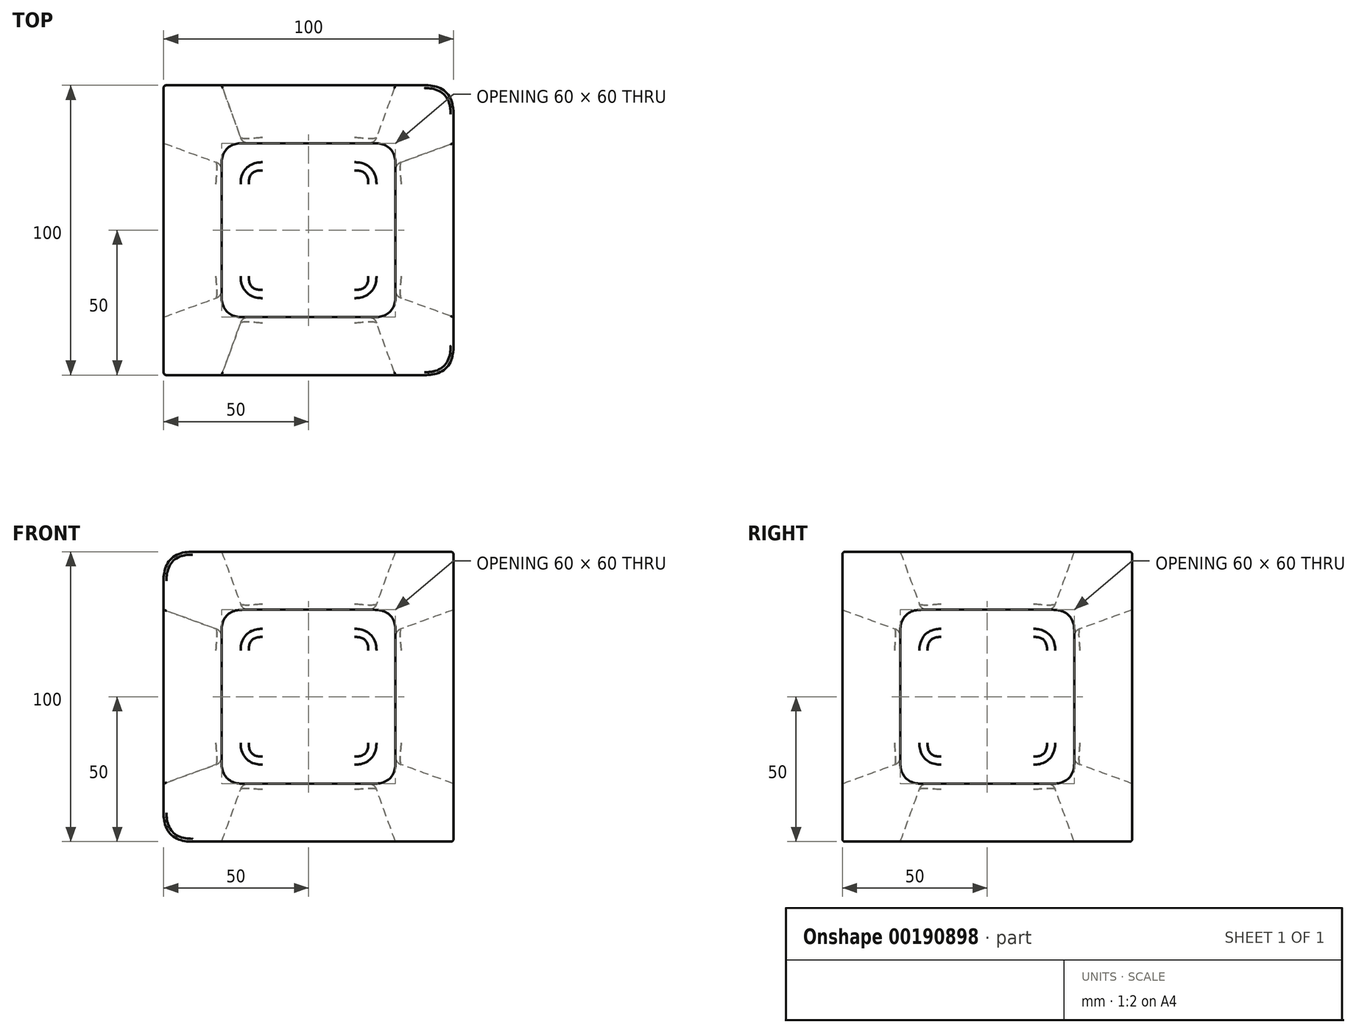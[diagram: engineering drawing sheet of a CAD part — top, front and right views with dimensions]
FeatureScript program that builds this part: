
annotation { "Feature Type Name" : "Feature", "Feature Type Description" : "" }
export const myFeature = defineFeature(function(context is Context, id is Id, definition is map)
    precondition{}
    {
        {
            var Q0;
            Q0=qCreatedBy(makeId("Top.planeOp"),FACE);
            var sketch = newSketch(context, id + "F0", { "sketchPlane" : qUnion([Q0])});
            skLineSegment(sketch, "E0.bottom", {"start": v(50, 50) * mm, "end": v(-50, 50) * mm});
            skLineSegment(sketch, "E0.top", {"start": v(50, -50) * mm, "end": v(-50, -50) * mm});
            skLineSegment(sketch, "E0.left", {"start": v(50, 50) * mm, "end": v(50, -50) * mm});
            skLineSegment(sketch, "E0.right", {"start": v(-50, 50) * mm, "end": v(-50, -50) * mm});
            skPoint(sketch, "E0.middle", {"position": v(0, 0) * mm});
            skSolve(sketch);
        }
        {
            var Q0;
            Q0 = qSketchRegion(id + "F0", true);
            extrude(context, id + "F1", {"entities" : qUnion([Q0]), "depth" : 100 * mm, "offsetDistance" : 25 * mm, "symmetric" : true});
        }
        {
            var Q0;
            Q0=makeQuery(id+"F1.opExtrude","CAP_FACE",FACE,{"disambiguationData":[OSD([sQuery(id+"F0.wireOp",EDGE,"E0.bottom"),sQuery(id+"F0.wireOp",EDGE,"E0.top"),sQuery(id+"F0.wireOp",EDGE,"E0.left"),sQuery(id+"F0.wireOp",EDGE,"E0.right")])],"isStart":false});
            var sketch = newSketch(context, id + "F2", { "sketchPlane" : qUnion([Q0])});
            skLineSegment(sketch, "E1.0", {"start": v(30, 30) * mm, "end": v(-30, 30) * mm});
            skLineSegment(sketch, "E1.1", {"start": v(30, 30) * mm, "end": v(30, -30) * mm});
            skLineSegment(sketch, "E1.2", {"start": v(30, -30) * mm, "end": v(-30, -30) * mm});
            skLineSegment(sketch, "E1.3", {"start": v(-30, 30) * mm, "end": v(-30, -30) * mm});
            skSolve(sketch);
        }
        {
            var Q0;
            Q0 = qSketchRegion(id + "F2", true);
            extrude(context, id + "F3", {"entities" : qUnion([Q0]), "operationType" : NewBodyOperationType.REMOVE, "oppositeDirection" : true, "depth" : 20 * mm, "offsetDistance" : 25 * mm, "hasDraft" : true, "draftAngle" : 20 * degree, "draftPullDirection" : true});
        }
        {
            var Q0;
            Q0=qCreatedBy(makeId("Top.planeOp"),FACE);
            var sketch = newSketch(context, id + "F4", { "sketchPlane" : qUnion([Q0])});
            skLineSegment(sketch, "E2", {"start": v(0, -64.23) * mm, "end": v(0, 63.51) * mm, "construction": true});
            skLineSegment(sketch, "E3", {"start": v(-60.37, 0) * mm, "end": v(65.94, 0) * mm, "construction": true});
            skSolve(sketch);
        }
        {
            var Q0;
            Q0=makeQuery(id+"F3.boolean.opBoolean","COPY",FACE,{"derivedFrom":makeQuery(id+"F3.opExtrude","CAP_FACE",FACE,{"disambiguationData":[OSD([sQuery(id+"F2.wireOp",EDGE,"E1.0"),sQuery(id+"F2.wireOp",EDGE,"E1.1"),sQuery(id+"F2.wireOp",EDGE,"E1.2"),sQuery(id+"F2.wireOp",EDGE,"E1.3")])],"isStart":false})});
            var Q1;
            Q1=makeQuery(id+"F3.boolean.opBoolean","COPY",FACE,{"derivedFrom":makeQuery(id+"F3.opExtrude","SWEPT_FACE",FACE,{"disambiguationData":[OSD([sQuery(id+"F2.wireOp",EDGE,"E1.3")])]})});
            var Q2;
            Q2=makeQuery(id+"F3.boolean.opBoolean","COPY",FACE,{"derivedFrom":makeQuery(id+"F3.opExtrude","SWEPT_FACE",FACE,{"disambiguationData":[OSD([sQuery(id+"F2.wireOp",EDGE,"E1.0")])]})});
            var Q3;
            Q3=makeQuery(id+"F3.boolean.opBoolean","COPY",FACE,{"derivedFrom":makeQuery(id+"F3.opExtrude","SWEPT_FACE",FACE,{"disambiguationData":[OSD([sQuery(id+"F2.wireOp",EDGE,"E1.1")])]})});
            var Q4;
            Q4=makeQuery(id+"F3.boolean.opBoolean","COPY",FACE,{"derivedFrom":makeQuery(id+"F3.opExtrude","SWEPT_FACE",FACE,{"disambiguationData":[OSD([sQuery(id+"F2.wireOp",EDGE,"E1.2")])]})});
            var Q5;
            Q5=sQuery(id+"F4.wireOp",EDGE,"E3");
            circularPattern(context, id + "F5", {"patternType" : PatternType.FACE, "faces" : qUnion([Q0, Q1, Q2, Q3, Q4]), "axis" : qUnion([Q5]), "angle" : 360 * degree, "instanceCount" : 4, "equalSpace" : true});
        }
        {
            var Q0;
            Q0=makeQuery(id+"F3.boolean.opBoolean","COPY",FACE,{"derivedFrom":makeQuery(id+"F3.opExtrude","CAP_FACE",FACE,{"disambiguationData":[OSD([sQuery(id+"F2.wireOp",EDGE,"E1.0"),sQuery(id+"F2.wireOp",EDGE,"E1.1"),sQuery(id+"F2.wireOp",EDGE,"E1.2"),sQuery(id+"F2.wireOp",EDGE,"E1.3")])],"isStart":false})});
            var Q1;
            Q1=makeQuery(id+"F3.boolean.opBoolean","COPY",FACE,{"derivedFrom":makeQuery(id+"F3.opExtrude","SWEPT_FACE",FACE,{"disambiguationData":[OSD([sQuery(id+"F2.wireOp",EDGE,"E1.3")])]})});
            var Q2;
            Q2=makeQuery(id+"F3.boolean.opBoolean","COPY",FACE,{"derivedFrom":makeQuery(id+"F3.opExtrude","SWEPT_FACE",FACE,{"disambiguationData":[OSD([sQuery(id+"F2.wireOp",EDGE,"E1.0")])]})});
            var Q3;
            Q3=makeQuery(id+"F3.boolean.opBoolean","COPY",FACE,{"derivedFrom":makeQuery(id+"F3.opExtrude","SWEPT_FACE",FACE,{"disambiguationData":[OSD([sQuery(id+"F2.wireOp",EDGE,"E1.1")])]})});
            var Q4;
            Q4=makeQuery(id+"F3.boolean.opBoolean","COPY",FACE,{"derivedFrom":makeQuery(id+"F3.opExtrude","SWEPT_FACE",FACE,{"disambiguationData":[OSD([sQuery(id+"F2.wireOp",EDGE,"E1.2")])]})});
            var Q5;
            Q5=sQuery(id+"F4.wireOp",EDGE,"E2");
            circularPattern(context, id + "F6", {"patternType" : PatternType.FACE, "faces" : qUnion([Q0, Q1, Q2, Q3, Q4]), "axis" : qUnion([Q5]), "angle" : 90 * degree, "instanceCount" : 2, "equalSpace" : true});
        }
        {
            var Q0;
            Q0=makeQuery(id+"F6.opPattern","COPY",FACE,{"derivedFrom":makeQuery(id+"F3.boolean.opBoolean","COPY",FACE,{"derivedFrom":makeQuery(id+"F3.opExtrude","CAP_FACE",FACE,{"disambiguationData":[OSD([sQuery(id+"F2.wireOp",EDGE,"E1.0"),sQuery(id+"F2.wireOp",EDGE,"E1.1"),sQuery(id+"F2.wireOp",EDGE,"E1.2"),sQuery(id+"F2.wireOp",EDGE,"E1.3")])],"isStart":false})}),"instanceName":"1"});
            var Q1;
            Q1=makeQuery(id+"F6.opPattern","COPY",FACE,{"derivedFrom":makeQuery(id+"F3.boolean.opBoolean","COPY",FACE,{"derivedFrom":makeQuery(id+"F3.opExtrude","SWEPT_FACE",FACE,{"disambiguationData":[OSD([sQuery(id+"F2.wireOp",EDGE,"E1.3")])]})}),"instanceName":"1"});
            var Q2;
            Q2=makeQuery(id+"F6.opPattern","COPY",FACE,{"derivedFrom":makeQuery(id+"F3.boolean.opBoolean","COPY",FACE,{"derivedFrom":makeQuery(id+"F3.opExtrude","SWEPT_FACE",FACE,{"disambiguationData":[OSD([sQuery(id+"F2.wireOp",EDGE,"E1.0")])]})}),"instanceName":"1"});
            var Q3;
            Q3=makeQuery(id+"F6.opPattern","COPY",FACE,{"derivedFrom":makeQuery(id+"F3.boolean.opBoolean","COPY",FACE,{"derivedFrom":makeQuery(id+"F3.opExtrude","SWEPT_FACE",FACE,{"disambiguationData":[OSD([sQuery(id+"F2.wireOp",EDGE,"E1.2")])]})}),"instanceName":"1"});
            var Q4;
            Q4=makeQuery(id+"F6.opPattern","COPY",FACE,{"derivedFrom":makeQuery(id+"F3.boolean.opBoolean","COPY",FACE,{"derivedFrom":makeQuery(id+"F3.opExtrude","SWEPT_FACE",FACE,{"disambiguationData":[OSD([sQuery(id+"F2.wireOp",EDGE,"E1.1")])]})}),"instanceName":"1"});
            var Q5;
            Q5=qCreatedBy(makeId("Right.planeOp"),FACE);
            mirror(context, id + "F7", {"patternType" : MirrorType.FACE, "faces" : qUnion([Q0, Q1, Q2, Q3, Q4]), "mirrorPlane" : qUnion([Q5])});
        }
        {
            var Q0;
            Q0=makeQuery(id+"F3.boolean.opBoolean","COPY",EDGE,{"derivedFrom":makeQuery(id+"F3.opExtrude","SWEPT_EDGE",EDGE,{"disambiguationData":[OSD([sQuery(id+"F2.wireOp",EDGE,"E1.0"),sQuery(id+"F2.wireOp",EDGE,"E1.3")])]})});
            var Q1;
            Q1=makeQuery(id+"F3.boolean.opBoolean","COPY",EDGE,{"derivedFrom":makeQuery(id+"F3.opExtrude","SWEPT_EDGE",EDGE,{"disambiguationData":[OSD([sQuery(id+"F2.wireOp",EDGE,"E1.0"),sQuery(id+"F2.wireOp",EDGE,"E1.1")])]})});
            var Q2;
            Q2=makeQuery(id+"F3.boolean.opBoolean","COPY",EDGE,{"derivedFrom":makeQuery(id+"F3.opExtrude","SWEPT_EDGE",EDGE,{"disambiguationData":[OSD([sQuery(id+"F2.wireOp",EDGE,"E1.2"),sQuery(id+"F2.wireOp",EDGE,"E1.3")])]})});
            var Q3;
            Q3=makeQuery(id+"F3.boolean.opBoolean","COPY",EDGE,{"derivedFrom":makeQuery(id+"F3.opExtrude","SWEPT_EDGE",EDGE,{"disambiguationData":[OSD([sQuery(id+"F2.wireOp",EDGE,"E1.1"),sQuery(id+"F2.wireOp",EDGE,"E1.2")])]})});
            var Q4;
            Q4=makeQuery(id+"F5.opPattern","COPY",EDGE,{"derivedFrom":makeQuery(id+"F3.boolean.opBoolean","COPY",EDGE,{"derivedFrom":makeQuery(id+"F3.opExtrude","SWEPT_EDGE",EDGE,{"disambiguationData":[OSD([sQuery(id+"F2.wireOp",EDGE,"E1.0"),sQuery(id+"F2.wireOp",EDGE,"E1.3")])]})}),"instanceName":"1"});
            var Q5;
            Q5=makeQuery(id+"F5.opPattern","COPY",EDGE,{"derivedFrom":makeQuery(id+"F3.boolean.opBoolean","COPY",EDGE,{"derivedFrom":makeQuery(id+"F3.opExtrude","SWEPT_EDGE",EDGE,{"disambiguationData":[OSD([sQuery(id+"F2.wireOp",EDGE,"E1.0"),sQuery(id+"F2.wireOp",EDGE,"E1.1")])]})}),"instanceName":"1"});
            var Q6;
            Q6=makeQuery(id+"F5.opPattern","COPY",EDGE,{"derivedFrom":makeQuery(id+"F3.boolean.opBoolean","COPY",EDGE,{"derivedFrom":makeQuery(id+"F3.opExtrude","SWEPT_EDGE",EDGE,{"disambiguationData":[OSD([sQuery(id+"F2.wireOp",EDGE,"E1.1"),sQuery(id+"F2.wireOp",EDGE,"E1.2")])]})}),"instanceName":"1"});
            var Q7;
            Q7=makeQuery(id+"F5.opPattern","COPY",EDGE,{"derivedFrom":makeQuery(id+"F3.boolean.opBoolean","COPY",EDGE,{"derivedFrom":makeQuery(id+"F3.opExtrude","SWEPT_EDGE",EDGE,{"disambiguationData":[OSD([sQuery(id+"F2.wireOp",EDGE,"E1.2"),sQuery(id+"F2.wireOp",EDGE,"E1.3")])]})}),"instanceName":"1"});
            var Q8;
            Q8=makeQuery(id+"F5.opPattern","COPY",EDGE,{"derivedFrom":makeQuery(id+"F3.boolean.opBoolean","COPY",EDGE,{"derivedFrom":makeQuery(id+"F3.opExtrude","SWEPT_EDGE",EDGE,{"disambiguationData":[OSD([sQuery(id+"F2.wireOp",EDGE,"E1.0"),sQuery(id+"F2.wireOp",EDGE,"E1.1")])]})}),"instanceName":"2"});
            var Q9;
            Q9=makeQuery(id+"F5.opPattern","COPY",EDGE,{"derivedFrom":makeQuery(id+"F3.boolean.opBoolean","COPY",EDGE,{"derivedFrom":makeQuery(id+"F3.opExtrude","SWEPT_EDGE",EDGE,{"disambiguationData":[OSD([sQuery(id+"F2.wireOp",EDGE,"E1.0"),sQuery(id+"F2.wireOp",EDGE,"E1.3")])]})}),"instanceName":"2"});
            var Q10;
            Q10=makeQuery(id+"F5.opPattern","COPY",EDGE,{"derivedFrom":makeQuery(id+"F3.boolean.opBoolean","COPY",EDGE,{"derivedFrom":makeQuery(id+"F3.opExtrude","SWEPT_EDGE",EDGE,{"disambiguationData":[OSD([sQuery(id+"F2.wireOp",EDGE,"E1.2"),sQuery(id+"F2.wireOp",EDGE,"E1.3")])]})}),"instanceName":"2"});
            var Q11;
            Q11=makeQuery(id+"F5.opPattern","COPY",EDGE,{"derivedFrom":makeQuery(id+"F3.boolean.opBoolean","COPY",EDGE,{"derivedFrom":makeQuery(id+"F3.opExtrude","SWEPT_EDGE",EDGE,{"disambiguationData":[OSD([sQuery(id+"F2.wireOp",EDGE,"E1.1"),sQuery(id+"F2.wireOp",EDGE,"E1.2")])]})}),"instanceName":"2"});
            var Q12;
            Q12=makeQuery(id+"F5.opPattern","COPY",EDGE,{"derivedFrom":makeQuery(id+"F3.boolean.opBoolean","COPY",EDGE,{"derivedFrom":makeQuery(id+"F3.opExtrude","SWEPT_EDGE",EDGE,{"disambiguationData":[OSD([sQuery(id+"F2.wireOp",EDGE,"E1.0"),sQuery(id+"F2.wireOp",EDGE,"E1.1")])]})}),"instanceName":"3"});
            var Q13;
            Q13=makeQuery(id+"F5.opPattern","COPY",EDGE,{"derivedFrom":makeQuery(id+"F3.boolean.opBoolean","COPY",EDGE,{"derivedFrom":makeQuery(id+"F3.opExtrude","SWEPT_EDGE",EDGE,{"disambiguationData":[OSD([sQuery(id+"F2.wireOp",EDGE,"E1.0"),sQuery(id+"F2.wireOp",EDGE,"E1.3")])]})}),"instanceName":"3"});
            var Q14;
            Q14=makeQuery(id+"F5.opPattern","COPY",EDGE,{"derivedFrom":makeQuery(id+"F3.boolean.opBoolean","COPY",EDGE,{"derivedFrom":makeQuery(id+"F3.opExtrude","SWEPT_EDGE",EDGE,{"disambiguationData":[OSD([sQuery(id+"F2.wireOp",EDGE,"E1.2"),sQuery(id+"F2.wireOp",EDGE,"E1.3")])]})}),"instanceName":"3"});
            var Q15;
            Q15=makeQuery(id+"F5.opPattern","COPY",EDGE,{"derivedFrom":makeQuery(id+"F3.boolean.opBoolean","COPY",EDGE,{"derivedFrom":makeQuery(id+"F3.opExtrude","SWEPT_EDGE",EDGE,{"disambiguationData":[OSD([sQuery(id+"F2.wireOp",EDGE,"E1.1"),sQuery(id+"F2.wireOp",EDGE,"E1.2")])]})}),"instanceName":"3"});
            var Q16;
            Q16=makeQuery(id+"F6.opPattern","COPY",EDGE,{"derivedFrom":makeQuery(id+"F3.boolean.opBoolean","COPY",EDGE,{"derivedFrom":makeQuery(id+"F3.opExtrude","SWEPT_EDGE",EDGE,{"disambiguationData":[OSD([sQuery(id+"F2.wireOp",EDGE,"E1.1"),sQuery(id+"F2.wireOp",EDGE,"E1.2")])]})}),"instanceName":"1"});
            var Q17;
            Q17=makeQuery(id+"F6.opPattern","COPY",EDGE,{"derivedFrom":makeQuery(id+"F3.boolean.opBoolean","COPY",EDGE,{"derivedFrom":makeQuery(id+"F3.opExtrude","SWEPT_EDGE",EDGE,{"disambiguationData":[OSD([sQuery(id+"F2.wireOp",EDGE,"E1.0"),sQuery(id+"F2.wireOp",EDGE,"E1.1")])]})}),"instanceName":"1"});
            var Q18;
            Q18=makeQuery(id+"F6.opPattern","COPY",EDGE,{"derivedFrom":makeQuery(id+"F3.boolean.opBoolean","COPY",EDGE,{"derivedFrom":makeQuery(id+"F3.opExtrude","SWEPT_EDGE",EDGE,{"disambiguationData":[OSD([sQuery(id+"F2.wireOp",EDGE,"E1.0"),sQuery(id+"F2.wireOp",EDGE,"E1.3")])]})}),"instanceName":"1"});
            var Q19;
            Q19=makeQuery(id+"F6.opPattern","COPY",EDGE,{"derivedFrom":makeQuery(id+"F3.boolean.opBoolean","COPY",EDGE,{"derivedFrom":makeQuery(id+"F3.opExtrude","SWEPT_EDGE",EDGE,{"disambiguationData":[OSD([sQuery(id+"F2.wireOp",EDGE,"E1.2"),sQuery(id+"F2.wireOp",EDGE,"E1.3")])]})}),"instanceName":"1"});
            var Q20;
            Q20=makeQuery(id+"F7.opPattern","COPY",EDGE,{"derivedFrom":makeQuery(id+"F6.opPattern","COPY",EDGE,{"derivedFrom":makeQuery(id+"F3.boolean.opBoolean","COPY",EDGE,{"derivedFrom":makeQuery(id+"F3.opExtrude","SWEPT_EDGE",EDGE,{"disambiguationData":[OSD([sQuery(id+"F2.wireOp",EDGE,"E1.2"),sQuery(id+"F2.wireOp",EDGE,"E1.3")])]})}),"instanceName":"1"}),"instanceName":"1"});
            var Q21;
            Q21=makeQuery(id+"F7.opPattern","COPY",EDGE,{"derivedFrom":makeQuery(id+"F6.opPattern","COPY",EDGE,{"derivedFrom":makeQuery(id+"F3.boolean.opBoolean","COPY",EDGE,{"derivedFrom":makeQuery(id+"F3.opExtrude","SWEPT_EDGE",EDGE,{"disambiguationData":[OSD([sQuery(id+"F2.wireOp",EDGE,"E1.0"),sQuery(id+"F2.wireOp",EDGE,"E1.3")])]})}),"instanceName":"1"}),"instanceName":"1"});
            var Q22;
            Q22=makeQuery(id+"F7.opPattern","COPY",EDGE,{"derivedFrom":makeQuery(id+"F6.opPattern","COPY",EDGE,{"derivedFrom":makeQuery(id+"F3.boolean.opBoolean","COPY",EDGE,{"derivedFrom":makeQuery(id+"F3.opExtrude","SWEPT_EDGE",EDGE,{"disambiguationData":[OSD([sQuery(id+"F2.wireOp",EDGE,"E1.0"),sQuery(id+"F2.wireOp",EDGE,"E1.1")])]})}),"instanceName":"1"}),"instanceName":"1"});
            var Q23;
            Q23=makeQuery(id+"F7.opPattern","COPY",EDGE,{"derivedFrom":makeQuery(id+"F6.opPattern","COPY",EDGE,{"derivedFrom":makeQuery(id+"F3.boolean.opBoolean","COPY",EDGE,{"derivedFrom":makeQuery(id+"F3.opExtrude","SWEPT_EDGE",EDGE,{"disambiguationData":[OSD([sQuery(id+"F2.wireOp",EDGE,"E1.1"),sQuery(id+"F2.wireOp",EDGE,"E1.2")])]})}),"instanceName":"1"}),"instanceName":"1"});
            fillet(context, id + "F8", {"entities" : qUnion([Q0, Q1, Q2, Q3, Q4, Q5, Q6, Q7, Q8, Q9, Q10, Q11, Q12, Q13, Q14, Q15, Q16, Q17, Q18, Q19, Q20, Q21, Q22, Q23]), "tangentPropagation" : true, "crossSection" : FilletCrossSection.CURVATURE, "radius" : 8 * mm, "magnitude" : 0.5, "defaultsChanged" : true, "vertexSettings" : []});
        }
        {
            var Q0;
            Q0=makeQuery(id+"F5.opPattern","COPY",FACE,{"derivedFrom":makeQuery(id+"F3.boolean.opBoolean","COPY",FACE,{"derivedFrom":makeQuery(id+"F3.opExtrude","CAP_FACE",FACE,{"disambiguationData":[OSD([sQuery(id+"F2.wireOp",EDGE,"E1.0"),sQuery(id+"F2.wireOp",EDGE,"E1.1"),sQuery(id+"F2.wireOp",EDGE,"E1.2"),sQuery(id+"F2.wireOp",EDGE,"E1.3")])],"isStart":false})}),"instanceName":"1"});
            var Q1;
            Q1=makeQuery(id+"F6.opPattern","COPY",FACE,{"derivedFrom":makeQuery(id+"F3.boolean.opBoolean","COPY",FACE,{"derivedFrom":makeQuery(id+"F3.opExtrude","CAP_FACE",FACE,{"disambiguationData":[OSD([sQuery(id+"F2.wireOp",EDGE,"E1.0"),sQuery(id+"F2.wireOp",EDGE,"E1.1"),sQuery(id+"F2.wireOp",EDGE,"E1.2"),sQuery(id+"F2.wireOp",EDGE,"E1.3")])],"isStart":false})}),"instanceName":"1"});
            var Q2;
            Q2=makeQuery(id+"F5.opPattern","COPY",FACE,{"derivedFrom":makeQuery(id+"F3.boolean.opBoolean","COPY",FACE,{"derivedFrom":makeQuery(id+"F3.opExtrude","CAP_FACE",FACE,{"disambiguationData":[OSD([sQuery(id+"F2.wireOp",EDGE,"E1.0"),sQuery(id+"F2.wireOp",EDGE,"E1.1"),sQuery(id+"F2.wireOp",EDGE,"E1.2"),sQuery(id+"F2.wireOp",EDGE,"E1.3")])],"isStart":false})}),"instanceName":"3"});
            var Q3;
            Q3=makeQuery(id+"F7.opPattern","COPY",FACE,{"derivedFrom":makeQuery(id+"F6.opPattern","COPY",FACE,{"derivedFrom":makeQuery(id+"F3.boolean.opBoolean","COPY",FACE,{"derivedFrom":makeQuery(id+"F3.opExtrude","CAP_FACE",FACE,{"disambiguationData":[OSD([sQuery(id+"F2.wireOp",EDGE,"E1.0"),sQuery(id+"F2.wireOp",EDGE,"E1.1"),sQuery(id+"F2.wireOp",EDGE,"E1.2"),sQuery(id+"F2.wireOp",EDGE,"E1.3")])],"isStart":false})}),"instanceName":"1"}),"instanceName":"1"});
            var Q4;
            Q4=makeQuery(id+"F3.boolean.opBoolean","COPY",FACE,{"derivedFrom":makeQuery(id+"F3.opExtrude","CAP_FACE",FACE,{"disambiguationData":[OSD([sQuery(id+"F2.wireOp",EDGE,"E1.0"),sQuery(id+"F2.wireOp",EDGE,"E1.1"),sQuery(id+"F2.wireOp",EDGE,"E1.2"),sQuery(id+"F2.wireOp",EDGE,"E1.3")])],"isStart":false})});
            var Q5;
            Q5=makeQuery(id+"F5.opPattern","COPY",FACE,{"derivedFrom":makeQuery(id+"F3.boolean.opBoolean","COPY",FACE,{"derivedFrom":makeQuery(id+"F3.opExtrude","CAP_FACE",FACE,{"disambiguationData":[OSD([sQuery(id+"F2.wireOp",EDGE,"E1.0"),sQuery(id+"F2.wireOp",EDGE,"E1.1"),sQuery(id+"F2.wireOp",EDGE,"E1.2"),sQuery(id+"F2.wireOp",EDGE,"E1.3")])],"isStart":false})}),"instanceName":"2"});
            fillet(context, id + "F9", {"entities" : qUnion([Q0, Q1, Q2, Q3, Q4, Q5]), "tangentPropagation" : true, "crossSection" : FilletCrossSection.CURVATURE, "radius" : 3 * mm, "magnitude" : 0.5, "defaultsChanged" : true, "vertexSettings" : []});
        }
        {
            var Q0;
            Q0=makeQuery(id+"F1.opExtrude","SWEPT_EDGE",EDGE,{"disambiguationData":[OSD([sQuery(id+"F0.wireOp",EDGE,"E0.top"),sQuery(id+"F0.wireOp",EDGE,"E0.left")])]});
            var Q1;
            Q1=makeQuery(id+"F1.opExtrude","CAP_EDGE",EDGE,{"disambiguationData":[OSD([sQuery(id+"F0.wireOp",EDGE,"E0.right")])],"isStart":false});
            var Q2;
            Q2=makeQuery(id+"F1.opExtrude","CAP_EDGE",EDGE,{"disambiguationData":[OSD([sQuery(id+"F0.wireOp",EDGE,"E0.right")])],"isStart":true});
            var Q3;
            Q3=makeQuery(id+"F1.opExtrude","SWEPT_EDGE",EDGE,{"disambiguationData":[OSD([sQuery(id+"F0.wireOp",EDGE,"E0.bottom"),sQuery(id+"F0.wireOp",EDGE,"E0.left")])]});
            fillet(context, id + "F10", {"entities" : qUnion([Q0, Q1, Q2, Q3]), "tangentPropagation" : true, "crossSection" : FilletCrossSection.CURVATURE, "radius" : 10 * mm, "magnitude" : 0.5, "defaultsChanged" : true, "vertexSettings" : []});
        }
        {
            var Q0;
            Q0=makeQuery(id+"F1.opExtrude","SWEPT_EDGE",EDGE,{"disambiguationData":[OSD([sQuery(id+"F0.wireOp",EDGE,"E0.top"),sQuery(id+"F0.wireOp",EDGE,"E0.right")])]});
            var Q1;
            Q1=makeQuery(id+"F6.opPattern","COPY",EDGE,{"derivedFrom":makeQuery(id+"F3.boolean.opBoolean","COPY",EDGE,{"derivedFrom":makeQuery(id+"F3.opExtrude","CAP_EDGE",EDGE,{"disambiguationData":[OSD([sQuery(id+"F2.wireOp",EDGE,"E1.0")])],"isStart":true})}),"instanceName":"1"});
            var Q2;
            Q2=makeQuery(id+"F5.opPattern","COPY",EDGE,{"derivedFrom":makeQuery(id+"F3.boolean.opBoolean","COPY",EDGE,{"derivedFrom":makeQuery(id+"F3.opExtrude","CAP_EDGE",EDGE,{"disambiguationData":[OSD([sQuery(id+"F2.wireOp",EDGE,"E1.3")])],"isStart":true})}),"instanceName":"1"});
            var Q3;
            Q3=makeQuery(id+"F5.opPattern","COPY",EDGE,{"derivedFrom":makeQuery(id+"F3.boolean.opBoolean","COPY",EDGE,{"derivedFrom":makeQuery(id+"F3.opExtrude","CAP_EDGE",EDGE,{"disambiguationData":[OSD([sQuery(id+"F2.wireOp",EDGE,"E1.1")])],"isStart":true})}),"instanceName":"3"});
            var Q4;
            Q4=makeQuery(id+"F7.opPattern","COPY",EDGE,{"derivedFrom":makeQuery(id+"F6.opPattern","COPY",EDGE,{"derivedFrom":makeQuery(id+"F3.boolean.opBoolean","COPY",EDGE,{"derivedFrom":makeQuery(id+"F3.opExtrude","CAP_EDGE",EDGE,{"disambiguationData":[OSD([sQuery(id+"F2.wireOp",EDGE,"E1.2")])],"isStart":true})}),"instanceName":"1"}),"instanceName":"1"});
            var Q5;
            Q5=makeQuery(id+"F3.boolean.opBoolean","COPY",EDGE,{"derivedFrom":makeQuery(id+"F3.opExtrude","CAP_EDGE",EDGE,{"disambiguationData":[OSD([sQuery(id+"F2.wireOp",EDGE,"E1.2")])],"isStart":true})});
            var Q6;
            Q6=makeQuery(id+"F5.opPattern","COPY",EDGE,{"derivedFrom":makeQuery(id+"F3.boolean.opBoolean","COPY",EDGE,{"derivedFrom":makeQuery(id+"F3.opExtrude","CAP_EDGE",EDGE,{"disambiguationData":[OSD([sQuery(id+"F2.wireOp",EDGE,"E1.0")])],"isStart":true})}),"instanceName":"2"});
            fillet(context, id + "F11", {"entities" : qUnion([Q0, Q1, Q2, Q3, Q4, Q5, Q6]), "tangentPropagation" : true, "crossSection" : FilletCrossSection.CURVATURE, "radius" : 1 * mm, "magnitude" : 0.5, "defaultsChanged" : false, "vertexSettings" : []});
        }
    });
